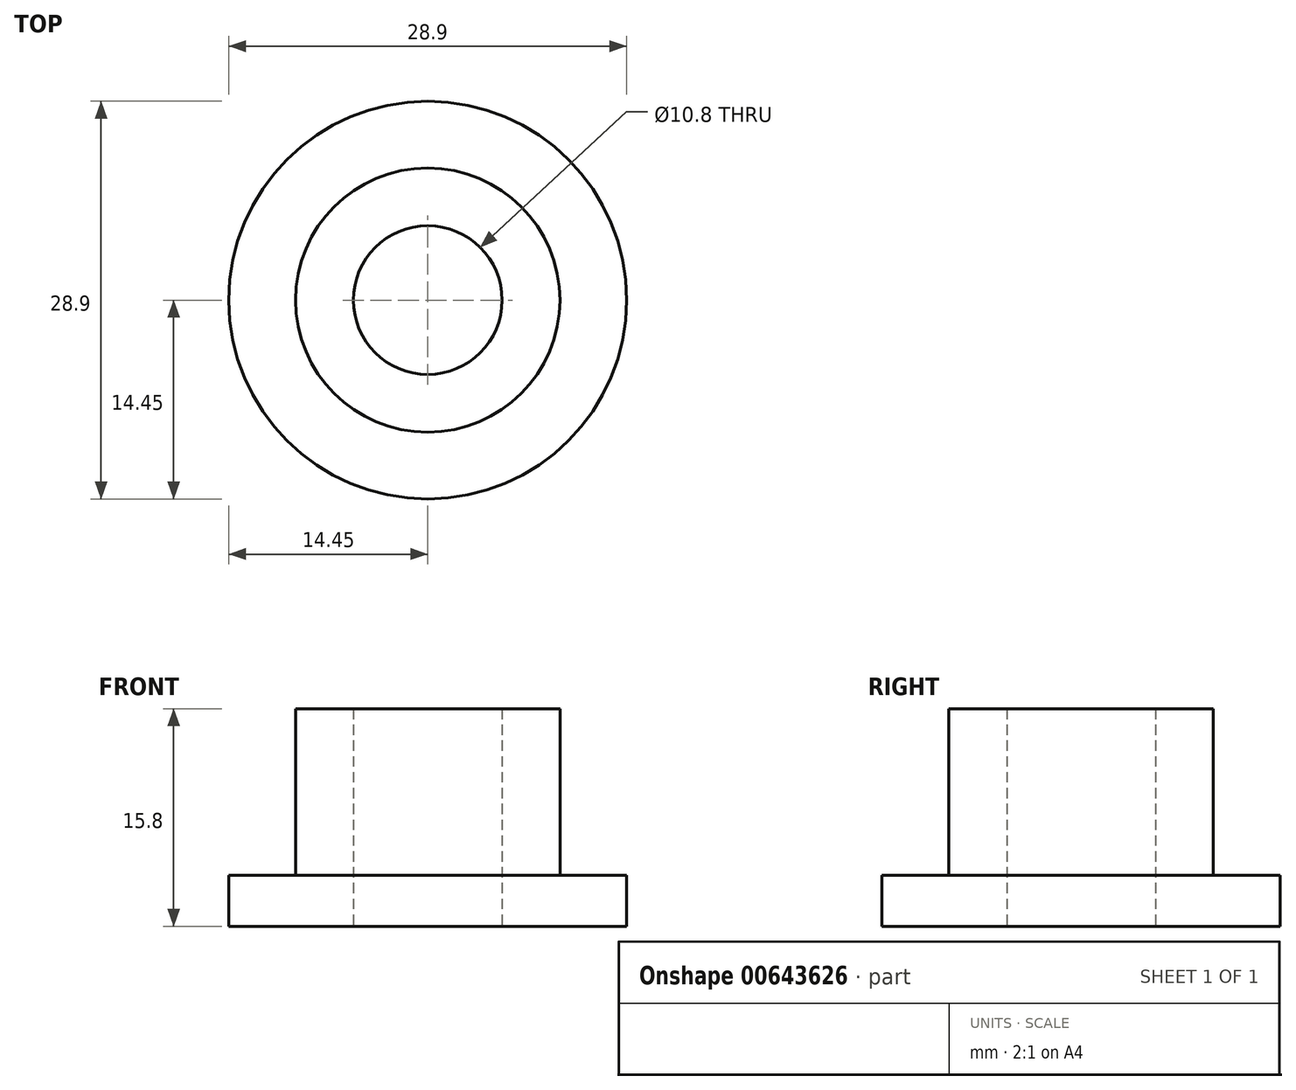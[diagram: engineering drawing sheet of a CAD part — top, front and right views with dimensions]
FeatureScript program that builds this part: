
annotation { "Feature Type Name" : "Feature", "Feature Type Description" : "" }
export const myFeature = defineFeature(function(context is Context, id is Id, definition is map)
    precondition{}
    {
        {
            var Q0;
            Q0=qCreatedBy(makeId("Top.planeOp"),FACE);
            var sketch = newSketch(context, id + "F0", { "sketchPlane" : qUnion([Q0])});
            skCircle(sketch, "E0", {"center": v(0, 0) * mm, "radius": 9.6 * mm});
            skSolve(sketch);
        }
        {
            var Q0;
            Q0 = qSketchRegion(id + "F0", true);
            extrude(context, id + "F1", {"entities" : qUnion([Q0]), "depth" : 15.8 * mm, "offsetDistance" : 25 * mm});
        }
        {
            var Q0;
            Q0=qCreatedBy(makeId("Top.planeOp"),FACE);
            var sketch = newSketch(context, id + "F2", { "sketchPlane" : qUnion([Q0])});
            skCircle(sketch, "E1", {"center": v(0, 0) * mm, "radius": 5.4 * mm});
            skSolve(sketch);
        }
        {
            var Q0;
            Q0 = qSketchRegion(id + "F2", true);
            extrude(context, id + "F3", {"entities" : qUnion([Q0]), "operationType" : NewBodyOperationType.REMOVE, "depth" : 20 * mm, "offsetDistance" : 25 * mm});
        }
        {
            var Q0;
            Q0=qCreatedBy(makeId("Top.planeOp"),FACE);
            var sketch = newSketch(context, id + "F4", { "sketchPlane" : qUnion([Q0])});
            skCircle(sketch, "E2", {"center": v(0, 0) * mm, "radius": 14.45 * mm});
            skSolve(sketch);
        }
        {
            var Q0;
            Q0 = qSketchRegion(id + "F4", true);
            extrude(context, id + "F5", {"entities" : qUnion([Q0]), "operationType" : NewBodyOperationType.ADD, "depth" : 3.7 * mm, "offsetDistance" : 25 * mm});
        }
        {
            var Q0;
            Q0=qCreatedBy(makeId("Top.planeOp"),FACE);
            var sketch = newSketch(context, id + "F6", { "sketchPlane" : qUnion([Q0])});
            skCircle(sketch, "E3", {"center": v(0, 0) * mm, "radius": 5.4 * mm});
            skSolve(sketch);
        }
        {
            var Q0;
            Q0 = qSketchRegion(id + "F6", true);
            extrude(context, id + "F7", {"entities" : qUnion([Q0]), "operationType" : NewBodyOperationType.REMOVE, "depth" : 3.7 * mm, "offsetDistance" : 25 * mm});
        }
    });
